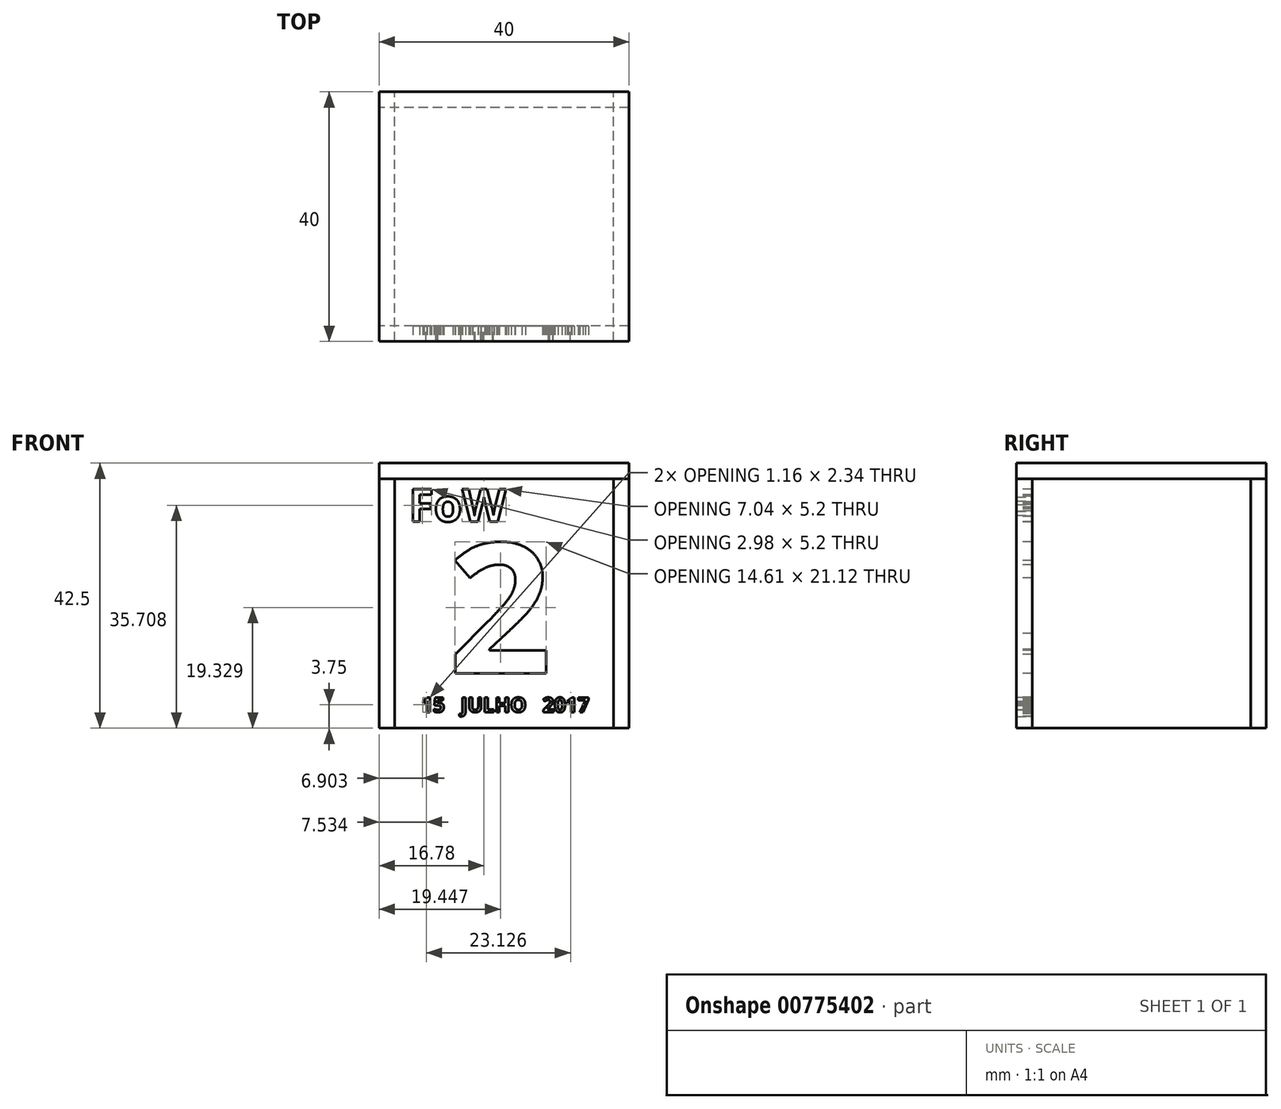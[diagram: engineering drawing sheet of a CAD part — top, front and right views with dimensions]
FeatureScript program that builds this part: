
annotation { "Feature Type Name" : "Feature", "Feature Type Description" : "" }
export const myFeature = defineFeature(function(context is Context, id is Id, definition is map)
    precondition{}
    {
        {
            var Q0;
            Q0=qCreatedBy(makeId("Top.planeOp"),FACE);
            var sketch = newSketch(context, id + "F0", { "sketchPlane" : qUnion([Q0])});
            skLineSegment(sketch, "E0.bottom", {"start": v(0, 0) * mm, "end": v(-40, 0) * mm});
            skLineSegment(sketch, "E0.top", {"start": v(0, 40) * mm, "end": v(-40, 40) * mm});
            skLineSegment(sketch, "E0.left", {"start": v(0, 0) * mm, "end": v(0, 40) * mm});
            skLineSegment(sketch, "E0.right", {"start": v(-40, 0) * mm, "end": v(-40, 40) * mm});
            skSolve(sketch);
        }
        {
            var Q0;
            Q0=qSketchRegion(id+"F0",true);
            extrude(context, id + "F1", {"entities" : qUnion([Q0]), "depth" : 2.5 * mm, "offsetDistance" : 25 * mm});
        }
        {
            var Q0;
            Q0=makeQuery(id+"F1.opExtrude","SWEPT_FACE",FACE,{"disambiguationData":[OSD([sQuery(id+"F0.wireOp",EDGE,"E0.bottom")])]});
            var sketch = newSketch(context, id + "F2", { "sketchPlane" : qUnion([Q0])});
            skLineSegment(sketch, "E1.bottom", {"start": v(-40, 0) * mm, "end": v(0, 0) * mm});
            skLineSegment(sketch, "E1.top", {"start": v(-40, -40) * mm, "end": v(0, -40) * mm});
            skLineSegment(sketch, "E1.left", {"start": v(-40, 0) * mm, "end": v(-40, -40) * mm});
            skLineSegment(sketch, "E1.right", {"start": v(0, 0) * mm, "end": v(0, -40) * mm});
            skSolve(sketch);
        }
        {
            var Q0;
            Q0=qSketchRegion(id+"F2",true);
            extrude(context, id + "F3", {"entities" : qUnion([Q0]), "oppositeDirection" : true, "depth" : 2.5 * mm, "offsetDistance" : 25 * mm});
        }
        {
            var Q0;
            Q0=makeQuery(id+"F1.opExtrude","SWEPT_FACE",FACE,{"disambiguationData":[OSD([sQuery(id+"F0.wireOp",EDGE,"E0.left")])]});
            var sketch = newSketch(context, id + "F4", { "sketchPlane" : qUnion([Q0])});
            skLineSegment(sketch, "E2.bottom", {"start": v(0, 0) * mm, "end": v(40, 0) * mm});
            skLineSegment(sketch, "E2.top", {"start": v(0, -40) * mm, "end": v(40, -40) * mm});
            skLineSegment(sketch, "E2.left", {"start": v(0, 0) * mm, "end": v(0, -40) * mm});
            skLineSegment(sketch, "E2.right", {"start": v(40, 0) * mm, "end": v(40, -40) * mm});
            skSolve(sketch);
        }
        {
            var Q0;
            Q0=qSketchRegion(id+"F4",true);
            extrude(context, id + "F5", {"entities" : qUnion([Q0]), "oppositeDirection" : true, "depth" : 2.5 * mm, "offsetDistance" : 25 * mm});
        }
        {
            var Q0;
            Q0=makeQuery(id+"F1.opExtrude","SWEPT_FACE",FACE,{"disambiguationData":[OSD([sQuery(id+"F0.wireOp",EDGE,"E0.top")])]});
            var sketch = newSketch(context, id + "F6", { "sketchPlane" : qUnion([Q0])});
            skLineSegment(sketch, "E3.bottom", {"start": v(0, 0) * mm, "end": v(40, 0) * mm});
            skLineSegment(sketch, "E3.top", {"start": v(0, -40) * mm, "end": v(40, -40) * mm});
            skLineSegment(sketch, "E3.left", {"start": v(0, 0) * mm, "end": v(0, -40) * mm});
            skLineSegment(sketch, "E3.right", {"start": v(40, 0) * mm, "end": v(40, -40) * mm});
            skSolve(sketch);
        }
        {
            var Q0;
            Q0=qSketchRegion(id+"F6",true);
            extrude(context, id + "F7", {"entities" : qUnion([Q0]), "oppositeDirection" : true, "depth" : 2.5 * mm, "offsetDistance" : 25 * mm});
        }
        {
            var Q0;
            Q0=makeQuery(id+"F1.opExtrude","SWEPT_FACE",FACE,{"disambiguationData":[OSD([sQuery(id+"F0.wireOp",EDGE,"E0.right")])]});
            var sketch = newSketch(context, id + "F8", { "sketchPlane" : qUnion([Q0])});
            skLineSegment(sketch, "E4.bottom", {"start": v(-40, 0) * mm, "end": v(0, 0) * mm});
            skLineSegment(sketch, "E4.top", {"start": v(-40, -40) * mm, "end": v(0, -40) * mm});
            skLineSegment(sketch, "E4.left", {"start": v(-40, 0) * mm, "end": v(-40, -40) * mm});
            skLineSegment(sketch, "E4.right", {"start": v(0, 0) * mm, "end": v(0, -40) * mm});
            skSolve(sketch);
        }
        {
            var Q0;
            Q0=qSketchRegion(id+"F8",true);
            extrude(context, id + "F9", {"entities" : qUnion([Q0]), "oppositeDirection" : true, "depth" : 2.5 * mm, "offsetDistance" : 25 * mm});
        }
        {
            var Q0;
            Q0=makeQuery(id+"F3.opExtrude","CAP_FACE",FACE,{"disambiguationData":[OSD([sQuery(id+"F2.wireOp",EDGE,"E1.bottom"),sQuery(id+"F2.wireOp",EDGE,"E1.top"),sQuery(id+"F2.wireOp",EDGE,"E1.left"),sQuery(id+"F2.wireOp",EDGE,"E1.right")])],"isStart":true});
            var sketch = newSketch(context, id + "F10", { "sketchPlane" : qUnion([Q0])});
            skText(sketch, "E5", { "text": "FoW", "fontName": "OpenSans-Bold.ttf"});
            skText(sketch, "E6", { "text": "2", "fontName": "OpenSans-Bold.ttf"});
            skText(sketch, "E7", { "text": "15   JULHO   2017", "fontName": "OpenSans-Bold.ttf"});
            const initialGuessF10  = {"E5": [-0.03524, -0.00689, 1, 0, 0.00524], "E6": [-0.02897, -0.03123, 1, 0, 0.021], "E7": [-0.03324, -0.03742, 1, 0, 0.00236]};
            skSetInitialGuess(sketch, initialGuessF10);
            skSolve(sketch);
        }
        {
            var Q0;
            Q0=qSketchRegion(id+"F10",true);
            extrude(context, id + "F11", {"entities" : qUnion([Q0]), "operationType" : NewBodyOperationType.REMOVE, "oppositeDirection" : true, "depth" : 3 * mm, "offsetDistance" : 25 * mm});
        }
    });
